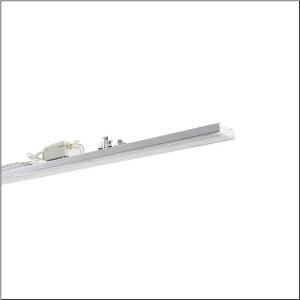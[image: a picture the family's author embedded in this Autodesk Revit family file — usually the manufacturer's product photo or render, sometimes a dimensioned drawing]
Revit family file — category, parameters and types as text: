
# Revit family: licross_r__21_recessed_mo_52tl197n48xg_c19d
name_source: partatom
category: Lighting Fixtures
units: mm (PartAtom-declared; Revit-internal decimal feet)

## family parameters
Cut with Voids When Loaded = No
Host = Face
Light Source = No
Part Type = Normal
Room Calculation Point = No
Round Connector Dimension = Use Diameter
Shared = No

## types (1)
- Licross® 21 Recessed MO (1 x LED, 8450 lm, 47.9 W, 4000K)
    Apparent Load = 48 VA
    CIE Flux Codes = 55 90 98 100 100
    Color Rendering = 80
    Color Temperature = 4000K
    Default Elevation = 1800 mm
    Description = Licross® 21 Recessed MO, luminaire insert, of sheet steel, galvanised, coil coated, white, length: 1.500mm, width: 66mm, height: 67mm, LED rated luminous flux: 8.450lm, light colour: 840, control gear: ON/OFF, with plug, 3-pole, with phase selection, mains connection: 220..240V, AC, 50/60Hz, rated input power: 48W, halogen-free wiring, primary light control with lens, of plastic, primary optical cover: cover, of PMMA, light emission: direct distribution, primary light characteristic: double asymmetric, protection rating (complete): IP40, insulation class (complete): insulation class I (protective earthing), certification: CE, ENEC, VDE, UKCA, protection symbol: D if used in an environment without relevant dust loads with corresponding accessories, impact resistance: IK06, permissible ambient temperature for indoor applications: -35..+40°C, corresponds to IFS (International Featured Standards) requirements for safety and quality in the food industry, reducing of maximum allowable ambient temperature of 5°C with ceiling mounting, LABS conformity tested according to VDMA 24364:2018-05, packaging unit: 1 piece
    Height = 58 mm
    Lamp = 1 x LED
    Lamp Light Flux = 8450 lm
    Lamp Power = 47.9 W
    Lamp count = 1
    Length = 1500 mm
    Luminous efficacy = 176 lm/W
    Manufacturer = Siteco
    ModVariant = No
    Model = 52TL197N48XG
    Mounting Place = Ceiling
    Mounting Type = Pendant
    Number of Poles = 1
    OnlyDefault = Yes
    Power Factor = 1
    Product Name = Licross® 21 Recessed MO
    Product group = luminaire insert
    ProductGroupID = 901
    Protection Class = Protection class I
    Protection Degree = IP 40
    RLX_Detail_Level = 1
    RLX_Emergency_Light_Flux = 0 lm
    RLX_Emergency_Type = 0
    RLX_Emergency_Type_DB = No
    RlxData = <blob elided: 20885 chars, md5=1fedbc61>
    Socket = socket
    Standby Power = 0 W
    System Light Flux = 8450 lm
    System Power = 48 W
    Type Comments = Product without accessories
    Type Image = l_1296930.jpg
    URL = http://relux.com
    VarID = ---
    Voltage = 0 V
    Weight = 0.00 kg
    Width = 66 mm

## geometry (parser evidence)
native form markers: Blend x4, Sweep x10
no freeform markers — native parametric forms only
